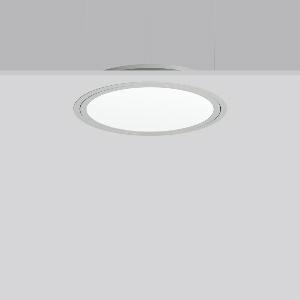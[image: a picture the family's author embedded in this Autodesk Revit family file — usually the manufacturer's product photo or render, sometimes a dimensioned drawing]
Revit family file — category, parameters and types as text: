
# Revit family: triona_round_e_312419_004_1_12_c620
name_source: partatom
category: Lighting Fixtures
units: mm (PartAtom-declared; Revit-internal decimal feet)

## family parameters
Cut with Voids When Loaded = No
Host = Face
Light Source = No
Part Type = Normal
Room Calculation Point = No
Round Connector Dimension = Use Diameter
Shared = No

## types (1)
- TRIONA round E (1 x LED Modul 840, 4900 lm, 4000)
    Apparent Load = 48 VA
    CIE Flux Codes = 49 80 96 100 100
    Color Rendering = 80
    Color Temperature = 4000
    Default Elevation = 1800 mm
    Description = Series: TRIONA round
Decorative round LED recessed surface luminaire. Cover made of sheet steel, powder-coated. Frame made of aluminium, powder-coated. Recessed ring: aluminium extrusion profile, powder coated. Light emission through a diffuser: plastic, opal. Lightguide and diffuser made of non-yellowing plastic (PMMA). Lateral light emission (RZB SIDELITE technology) for above-average homogeneous light distribution. Suitable for installation in cavity ceilings. Tool-free mounting system thanks to the rocker arm mechanism (patent pending). Electronic ballast included. Very easy installation thanks to Plug+Play connection. 
Colour: silver, matt (approx. RAL 9006)
Diameter: 505 mm
Height: 2 mm
Cut-out diameter: 482 mm
Recess height: 100 mm
Luminaire: recess height: 89 mm
Lamp: LED
Socket: without socket
Colour temperature: 4000K
Colour rendering index (CRI): 80
System power: 48 W
Rated luminous flux: 4900 lm
Luminous efficiency: 102 lm/W
Control gear: Converter, dimmable, DALI
Protection class: I
Type of protection: IP 40
    Height = 0 mm  [stored 0 ft]
    Lamp = 1 x LED Modul 840
    Lamp Light Flux = 4900 lm
    Lamp count = 1
    Length = 505 mm
    Lifetime = 50000 h
    Luminous efficacy = 102 lm/W
    Manufacturer = RZB
    ModVariant = No
    Model = 312419.004.1.12
    Mounting Place = Ceiling
    Mounting Type = Recessed
    Number of Poles = 1
    OnlyDefault = Yes
    Power Factor = 1
    Product Name = TRIONA round E
    Product group = Recessed modular luminaires
    ProductGroupID = 406
    Protection Class = Protection class I
    Protection Degree = IP 20
    RLX_Detail_Level = 1
    RLX_Emergency_Light_Flux = 0 lm
    RLX_Emergency_Type = 0
    RLX_Emergency_Type_DB = No
    RlxData = <blob elided: 31393 chars, md5=29b02970>
    Socket = socket
    Standby Power = 0 W
    System Light Flux = 4900 lm
    System Power = 48 W
    Type Comments = Product without accessories
    Type Image = 312419.004.12.jpg
    URL = http://relux.com
    VarID = ---
    Voltage = 230 V
    Voltage Range = 220-240 V
    Weight = 0.00 kg
    Width = 0 mm  [stored 0 ft]

note: [stored X ft] marks values corroborated as IEEE doubles in the binary element streams (Revit-internal decimal feet)

## geometry (parser evidence)
native form markers: Blend x4, Sweep x11
no freeform markers — native parametric forms only
